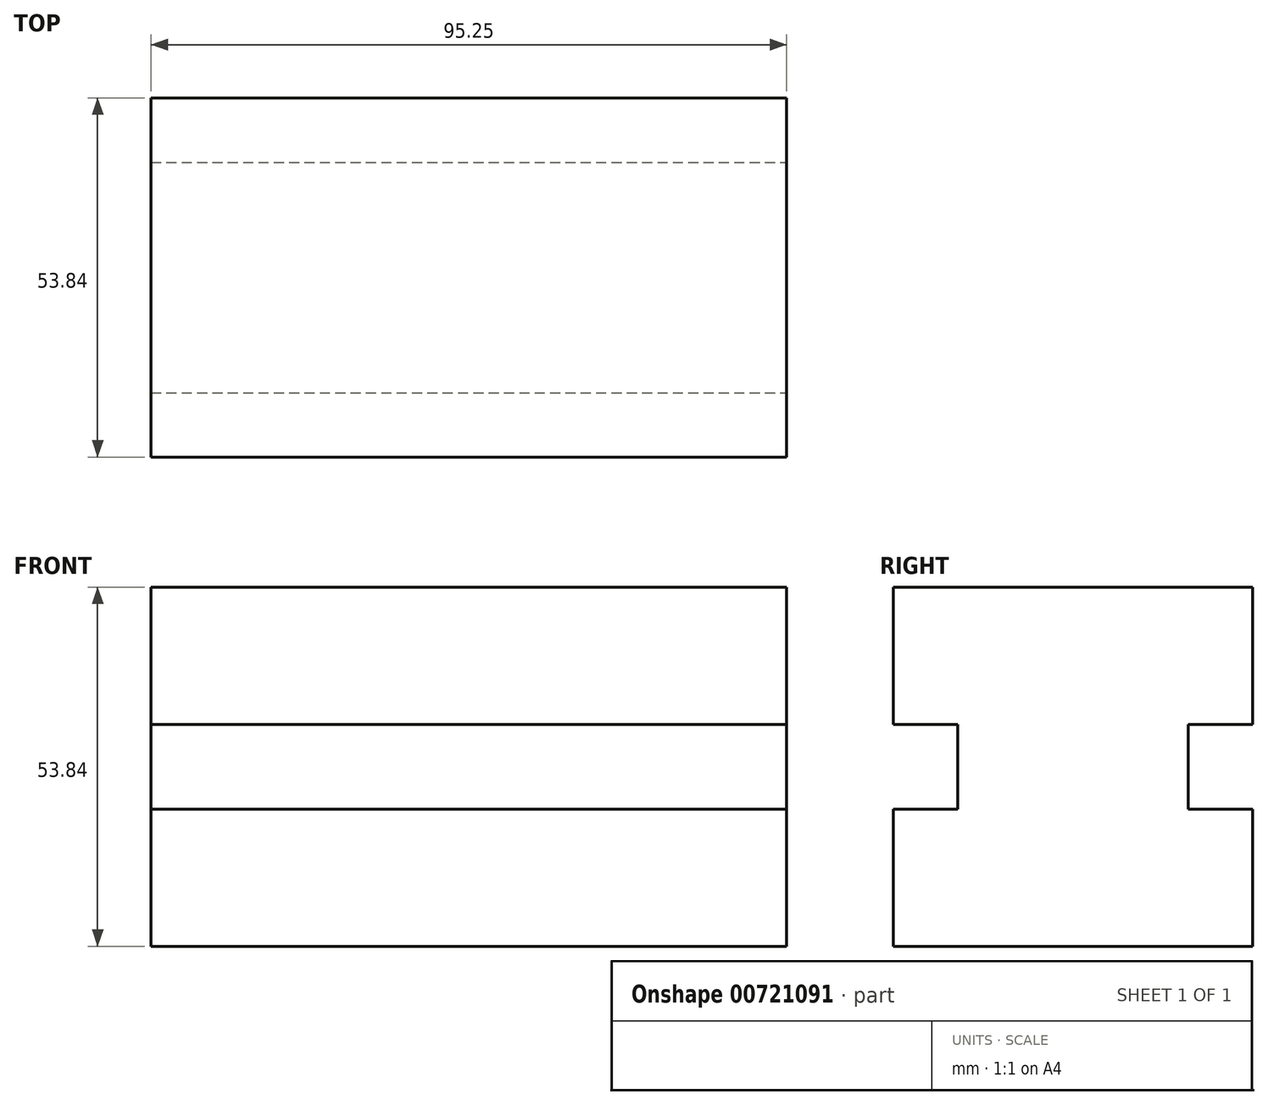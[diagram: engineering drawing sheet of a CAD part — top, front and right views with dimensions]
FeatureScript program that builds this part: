
annotation { "Feature Type Name" : "Feature", "Feature Type Description" : "" }
export const myFeature = defineFeature(function(context is Context, id is Id, definition is map)
    precondition{}
    {
        {
            var Q0;
            Q0=qCreatedBy(makeId("Right.planeOp"),FACE);
            var sketch = newSketch(context, id + "F0", { "sketchPlane" : qUnion([Q0])});
            skLineSegment(sketch, "E0.bottom", {"start": v(26.92, -26.92) * mm, "end": v(-26.92, -26.92) * mm});
            skLineSegment(sketch, "E0.top", {"start": v(26.92, 26.92) * mm, "end": v(-26.92, 26.92) * mm});
            skLineSegment(sketch, "E0.left", {"start": v(26.92, -26.92) * mm, "end": v(26.92, -6.35) * mm});
            skLineSegment(sketch, "E0.right", {"start": v(-26.92, -26.92) * mm, "end": v(-26.92, -6.35) * mm});
            skPoint(sketch, "E0.middle", {"position": v(0, 0) * mm});
            skLineSegment(sketch, "E1.bottom", {"start": v(-26.92, 6.35) * mm, "end": v(-17.27, 6.35) * mm});
            skLineSegment(sketch, "E1.top", {"start": v(-26.92, -6.35) * mm, "end": v(-17.27, -6.35) * mm});
            skLineSegment(sketch, "E1.right", {"start": v(-17.27, 6.35) * mm, "end": v(-17.27, -6.35) * mm});
            skLineSegment(sketch, "E2", {"start": v(0, 34.07) * mm, "end": v(0, -57.8) * mm, "construction": true});
            skPoint(sketch, "E2.startSnap0", {"position": v(0, 26.92) * mm});
            skPoint(sketch, "E2.endSnap0", {"position": v(0, -26.92) * mm});
            skLineSegment(sketch, "E3.MirrorCS", {"start": v(26.92, 6.35) * mm, "end": v(17.27, 6.35) * mm});
            skLineSegment(sketch, "E4.MirrorCS", {"start": v(26.92, -6.35) * mm, "end": v(17.27, -6.35) * mm});
            skLineSegment(sketch, "E5.MirrorCS", {"start": v(17.27, 6.35) * mm, "end": v(17.27, -6.35) * mm});
            skLineSegment(sketch, "E6.trimOffspring", {"start": v(-26.92, 6.35) * mm, "end": v(-26.92, 26.92) * mm});
            skLineSegment(sketch, "E7.trimOffspring", {"start": v(26.92, 6.35) * mm, "end": v(26.92, 26.92) * mm});
            skSolve(sketch);
        }
        {
            var Q0;
            Q0=makeQuery(id+"F0.imprint","IMPRINT",FACE,{"disambiguationData":[TD([[makeQuery(id+"F0.imprint","IMPRINT",EDGE,{"derivedFrom":sQuery(id+"F0.wireOp",EDGE,"E0.bottom")}),-1.0]])]});
            extrude(context, id + "F1", {"entities" : qUnion([Q0]), "oppositeDirection" : true, "depth" : 95.25 * mm, "offsetDistance" : 25.4 * mm});
        }
    });
